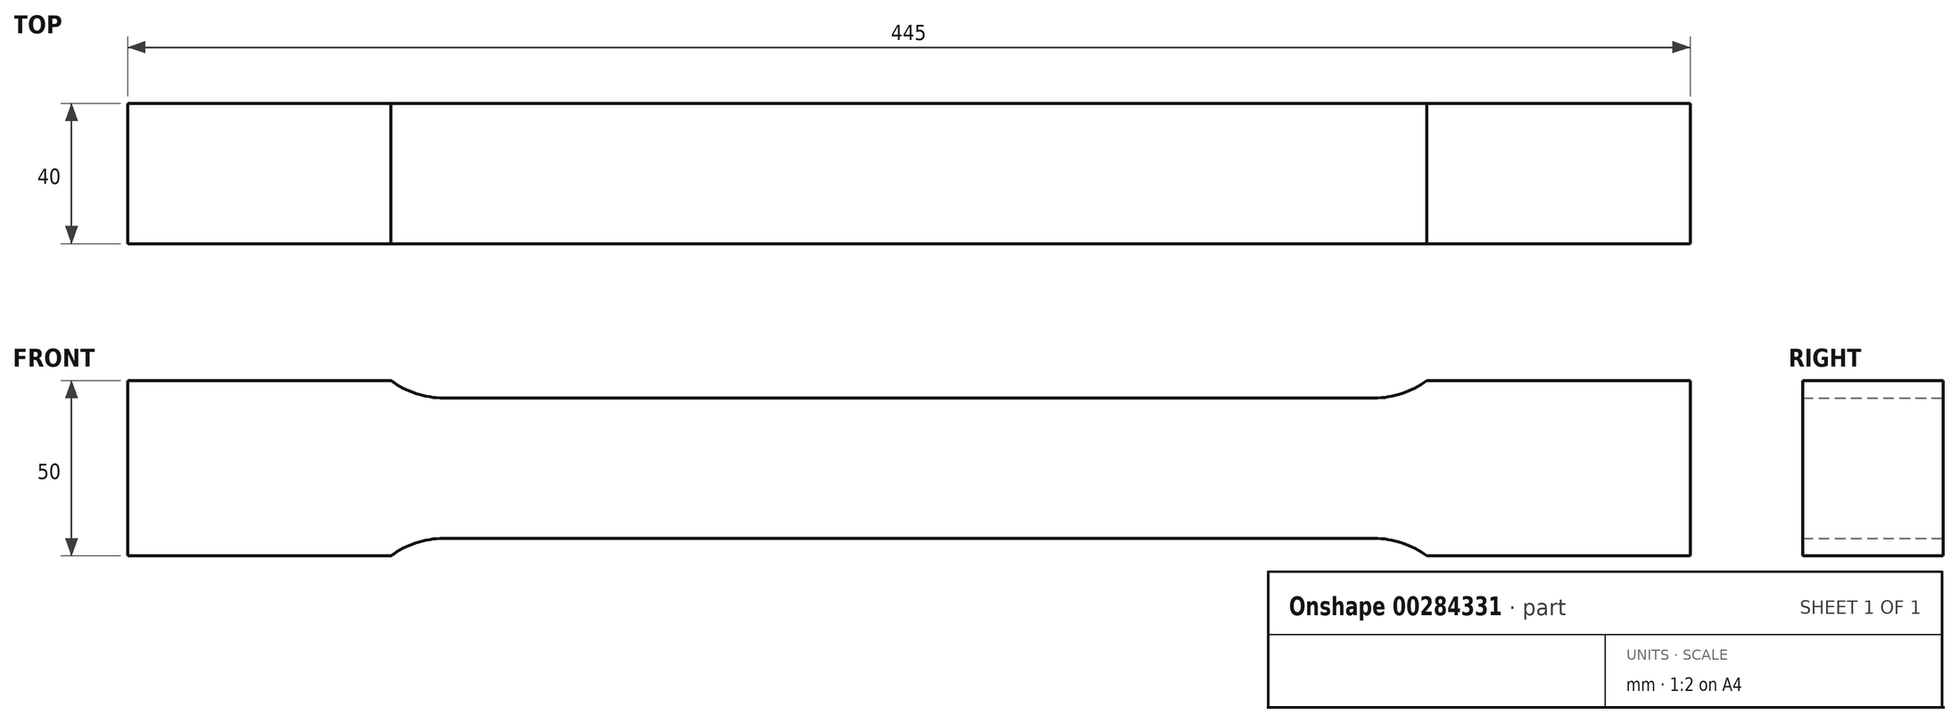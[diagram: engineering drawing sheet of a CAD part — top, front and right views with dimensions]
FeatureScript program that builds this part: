
annotation { "Feature Type Name" : "Feature", "Feature Type Description" : "" }
export const myFeature = defineFeature(function(context is Context, id is Id, definition is map)
    precondition{}
    {
        {
            var Q0;
            Q0=qCreatedBy(makeId("Front.planeOp"),FACE);
            var sketch = newSketch(context, id + "F0", { "sketchPlane" : qUnion([Q0])});
            skLineSegment(sketch, "E0", {"start": v(0, 20) * mm, "end": v(132.5, 20) * mm});
            skArc(sketch, "E1", {"start": v(132.5, 20) * mm, "mid": v(140.4, 21.28) * mm, "end": v(147.5, 25) * mm});
            skLineSegment(sketch, "E2", {"start": v(147.5, 25) * mm, "end": v(222.5, 25) * mm});
            skLineSegment(sketch, "E3", {"start": v(222.5, 25) * mm, "end": v(222.5, 0) * mm});
            skLineSegment(sketch, "E4.MirrorCS", {"start": v(0, -20) * mm, "end": v(132.5, -20) * mm});
            skLineSegment(sketch, "E5.MirrorCS", {"start": v(222.5, -25) * mm, "end": v(222.5, 0) * mm});
            skLineSegment(sketch, "E6.MirrorCS", {"start": v(147.5, -25) * mm, "end": v(222.5, -25) * mm});
            skArc(sketch, "E7.MirrorCS", {"start": v(132.5, -20) * mm, "mid": v(140.4, -21.28) * mm, "end": v(147.5, -25) * mm});
            skArc(sketch, "E8.MirrorCS", {"start": v(-132.5, -20) * mm, "mid": v(-140.4, -21.28) * mm, "end": v(-147.5, -25) * mm});
            skLineSegment(sketch, "E9.MirrorCS", {"start": v(-147.5, -25) * mm, "end": v(-222.5, -25) * mm});
            skLineSegment(sketch, "E10.MirrorCS", {"start": v(0, 20) * mm, "end": v(-132.5, 20) * mm});
            skArc(sketch, "E11.MirrorCS", {"start": v(-132.5, 20) * mm, "mid": v(-140.4, 21.28) * mm, "end": v(-147.5, 25) * mm});
            skLineSegment(sketch, "E12.MirrorCS", {"start": v(-147.5, 25) * mm, "end": v(-222.5, 25) * mm});
            skLineSegment(sketch, "E13.MirrorCS", {"start": v(-222.5, -25) * mm, "end": v(-222.5, 0) * mm});
            skLineSegment(sketch, "E14.MirrorCS", {"start": v(-222.5, 25) * mm, "end": v(-222.5, 0) * mm});
            skLineSegment(sketch, "E15.MirrorCS", {"start": v(0, -20) * mm, "end": v(-132.5, -20) * mm});
            skSolve(sketch);
        }
        {
            var Q0;
            Q0 = qSketchRegion(id + "F0", true);
            extrude(context, id + "F1", {"entities" : qUnion([Q0]), "endBound" : BoundingType.SYMMETRIC, "depth" : 40 * mm});
        }
    });
